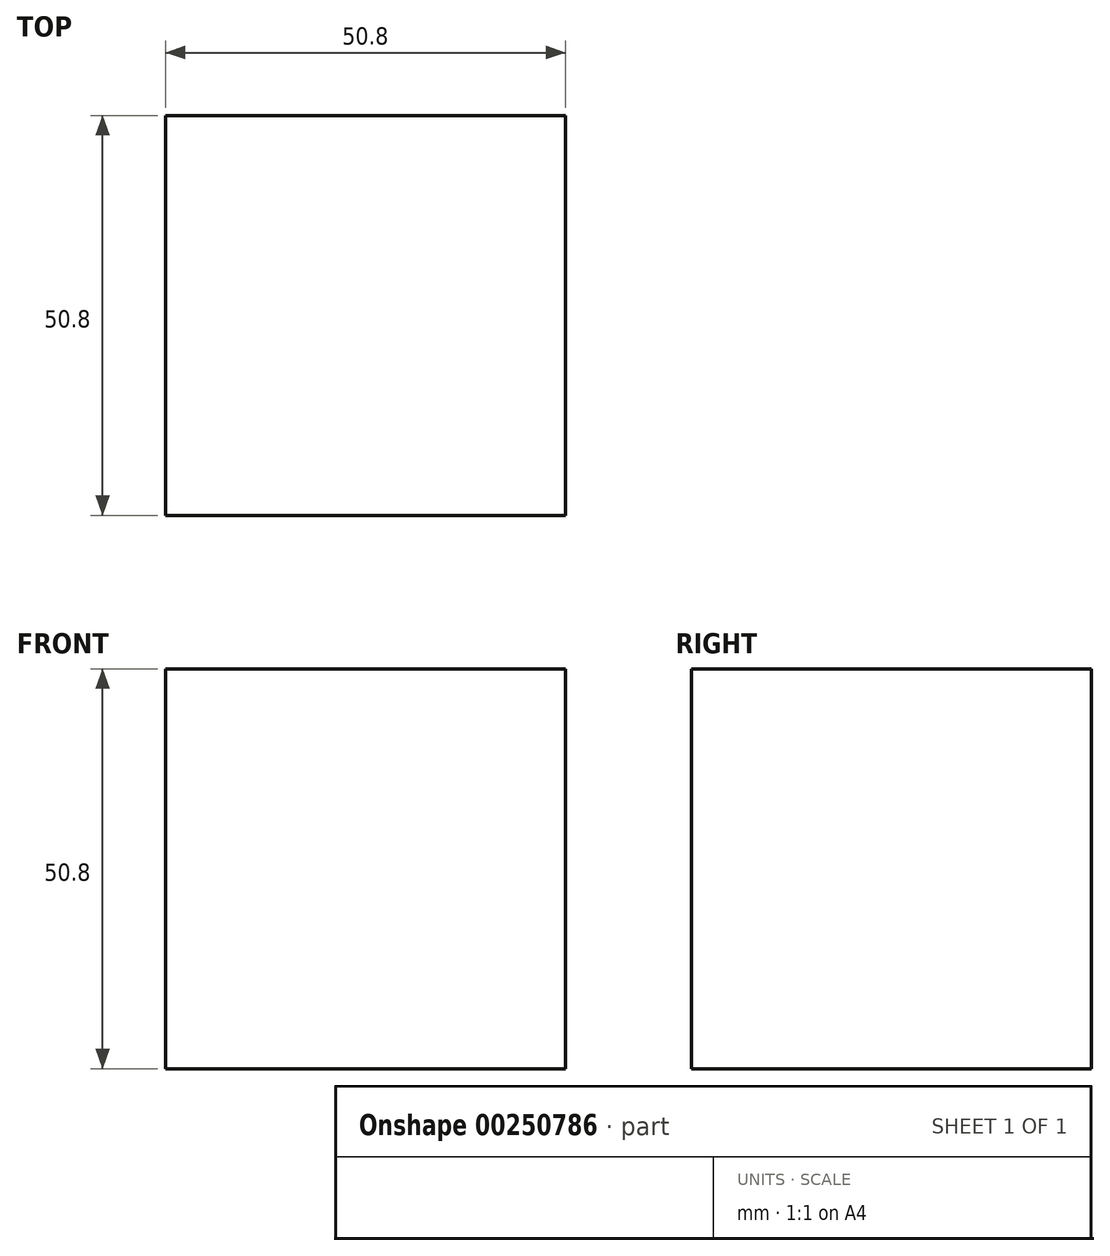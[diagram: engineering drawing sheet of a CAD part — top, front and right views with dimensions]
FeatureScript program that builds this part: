
annotation { "Feature Type Name" : "Feature", "Feature Type Description" : "" }
export const myFeature = defineFeature(function(context is Context, id is Id, definition is map)
    precondition{}
    {
        {
            var Q0;
            Q0=qCreatedBy(makeId("Front.planeOp"),FACE);
            var sketch = newSketch(context, id + "F0", { "sketchPlane" : qUnion([Q0])});
            skLineSegment(sketch, "E0.bottom", {"start": v(25.4, 25.4) * mm, "end": v(-25.4, 25.4) * mm});
            skLineSegment(sketch, "E0.top", {"start": v(25.4, -25.4) * mm, "end": v(-25.4, -25.4) * mm});
            skLineSegment(sketch, "E0.left", {"start": v(25.4, 25.4) * mm, "end": v(25.4, -25.4) * mm});
            skLineSegment(sketch, "E0.right", {"start": v(-25.4, 25.4) * mm, "end": v(-25.4, -25.4) * mm});
            skPoint(sketch, "E0.middle", {"position": v(0, 0) * mm});
            skSolve(sketch);
        }
        {
            var Q0;
            Q0=sQuery(id+"F0.wireOp",EDGE,"E0.bottom");
            var Q1;
            Q1=sQuery(id+"F0.wireOp",EDGE,"E0.right");
            var Q2;
            Q2=sQuery(id+"F0.wireOp",EDGE,"E0.left");
            var Q3;
            Q3=sQuery(id+"F0.wireOp",EDGE,"E0.top");
            extrude(context, id + "F1", {"bodyType" : ToolBodyType.SURFACE, "surfaceEntities" : qUnion([Q0, Q1, Q2, Q3]), "endBound" : BoundingType.SYMMETRIC, "depth" : 50.8 * mm});
        }
    });
